# Revit family: B30
name_source: partatom
category: Lighting Fixtures
units: mm (PartAtom-declared; Revit-internal decimal feet)

## family parameters
Always vertical = Yes
Cut with Voids When Loaded = No
Light Source = Yes
OmniClass Number = 23.80.70.14
OmniClass Title = Luminaries for External Lighting
Part Type = Normal
Room Calculation Point = No
Round Connector Dimension = Use Diameter
Shared = No
Work Plane-Based = No

## types (1)
- B30
    Apparent Load = 0 VA
    Assembly Code = D5020200
    Color Filter = 16777215
    Default Elevation = 0' - 0"
    Description = The B30 Traditional Bollard is clean, simple and precise. The exclusive Kim optical louver system achieves broad light distribution with low glare yet high visibility.

Exclusive Kim optical louver system achieves a broad distribution with low glare
Battery back-up, emergency battery pack and houseside shield options
    Diameter = 0' - 8"
    Dimming Lamp Color Temperature Shift = <None>
    Finish = Powder Coat-Black
    Glass = GlassTemper Molded
    Height = 3' - 6"
    Lamp = LED
    Load Classification = Lighting
    Manufacturer = Kim Lighting
    MasterFormat Title = Landscape Lighting, Site Lighting, Walkway Lighting
    Model = B30 Traditional Bollards
    Number of Poles = 1
    Photometric Notes = More IES files download on Photometric Web Link
    Photometric Web File = b30-8r-10l3k.ies
    Power Factor = 1
    Radius = 0' - 4"
    Series = Traditional Bollards
    Tilt Angle = 90.00°
    Type Comments = Lighted Bollard
    URL = https://www.currentlighting.com
    Voltage = 120 V
    Wattage Comments = default

## geometry (parser evidence)
native form markers: Sweep x3
no freeform markers — native parametric forms only
